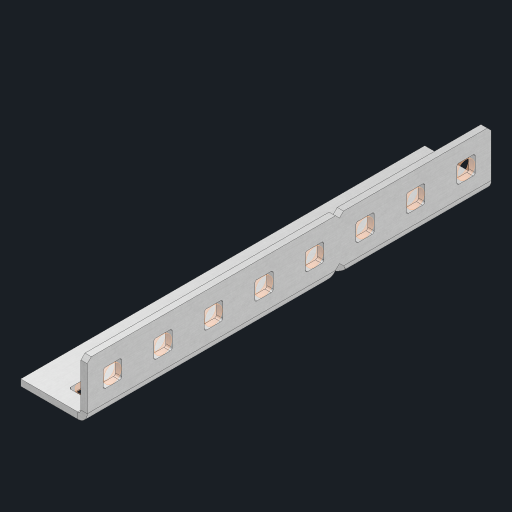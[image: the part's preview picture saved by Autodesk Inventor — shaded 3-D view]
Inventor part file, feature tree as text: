
AUTODESK INVENTOR PART (.ipt)
format: ipt  version: 2023 (Build 270158000, 158)  size: 471,552 bytes
history: native  units: in
note: dims shown in document units (in); Inventor stores cm internally (conversion verified against a paired STEP export)
features: other x21, extrude x15, sheet_metal_op x10, sketch x8, mirror x1, pattern_linear x1, chamfer x1
ambient origin geometry x8: Origin, YZ Plane, XZ Plane, XY Plane, X Axis, Y Axis, Z Axis, Center Point
bodies: Solid1 (feature_tree), Body (feature_tree)
feature tree (57):
  other  "Flange Pattern Plane"
  sheet_metal_op  "Flange Pattern"
  sheet_metal_op  "Body Pattern"
  other  "Arc Length"
  mirror  "Notch Mirror"
  pattern_linear  "Notch Pattern"  Spacing1=0.25in  [1 undecoded]
  chamfer  "End Chamfer"
  extrude  "Half Cut"  Depth=0.0625in
  sketch  "Sketch1"  dims[d0=1.5in]
  other  "Plate1"
  sketch  "Sketch2"  dims[d1=4.0in]
  other  "Plate2"
  sheet_metal_op  "Bend1"
  sheet_metal_op  "Corner1"
  sketch  "Sketch3"  dims[d2=0.0625in]
  other  "Flange Pattern Sketch"
  sketch  "Sketch7"  dims[d3=0.0625in]
  other  "Srf1"
  other  "Srf2"
  sketch  "Sketch8"  dims[d4=0.0312in]
  sketch  "Sketch9"  dims[d5=0.125in]
  other  "Srf91"
  sheet_metal_op  "Body Pattern Sketch"
  other  "Srf92"
  sketch  "Sketch13"  dims[d6=0.0625in]
  sketch  "Sketch14"  dims[d7=0.5in d8=90.0deg d9=0.0312in d10=0.25in d11=0.0625in d12=0.0625in d16=0.182in d17=0.02in d18=0.0625in d19=0.0in d20=0.25in d21=0.25in d46=0.172in d47=1.0in d48=0.0in d49=0.182in d50=0.02in d51=0.25in d52=0.25in d53=0.0625in d54=0.0in d55=0.172in d56=1.0in d57=0.0in d60=3.1496in d62=0.5in d63=0.3937in d65=0.5in d85=0.1473in d86=0.1782in d88=0.04in d89=0.0625in d90=0.0in d91=0.04in d92=0.0491in d95=2.5in d96=0.04in d97=0.25in d98=45.0deg d101=0.0in d102=2.497in d131=0.5in d132=3.1496in d134=0.5in d139=0.5in]
  other  "Srf856"
  other  "Srf1310"
  other  "Srf1311"
  other  "Srf1312"
  other  "Srf1376"
  other  "Srf1377"
  other  "Srf1728"
  other  "Srf1755"
  other  "Srf1878"
  other  "Srf1879"
  other  "Srf1942"
  other  "Srf1943"
  sheet_metal_op  "Flange Stamp"
  sheet_metal_op  "Flange Circle"
  sheet_metal_op  "Body Stamp"
  sheet_metal_op  "Body Circle"
  sheet_metal_op  "Notch"
  extrude  "ExtrusionSrf2"  Depth=0.0625in
  extrude  "ExtrusionSrf92"  Depth=0.5in
  extrude  "ExtrusionSrf856"  Depth=0.02in
  extrude  "ExtrusionSrf1310"  Depth=0.0625in
  extrude  "ExtrusionSrf1311"  TaperAngle=0.0deg  [1 undecoded]
  extrude  "ExtrusionSrf1312"  Depth=0.5in
  extrude  "ExtrusionSrf1376"  Depth=0.5in
  extrude  "ExtrusionSrf1377"  Depth=0.5in
  extrude  "ExtrusionSrf1728"  Depth=0.5in TaperAngle=0.0deg
  extrude  "ExtrusionSrf1755"  Depth=0.5in
  extrude  "ExtrusionSrf1878"  Depth=0.02in
  extrude  "ExtrusionSrf1879"  Depth=0.5in
  extrude  "ExtrusionSrf1942"  Depth=0.5in
  extrude  "ExtrusionSrf1943"  Depth=0.0625in
note: 2 required parameter values undecoded (feature->parameter linkage not recoverable at this tier; creation-order binding heuristic only, values carry confidence <= 0.55)
